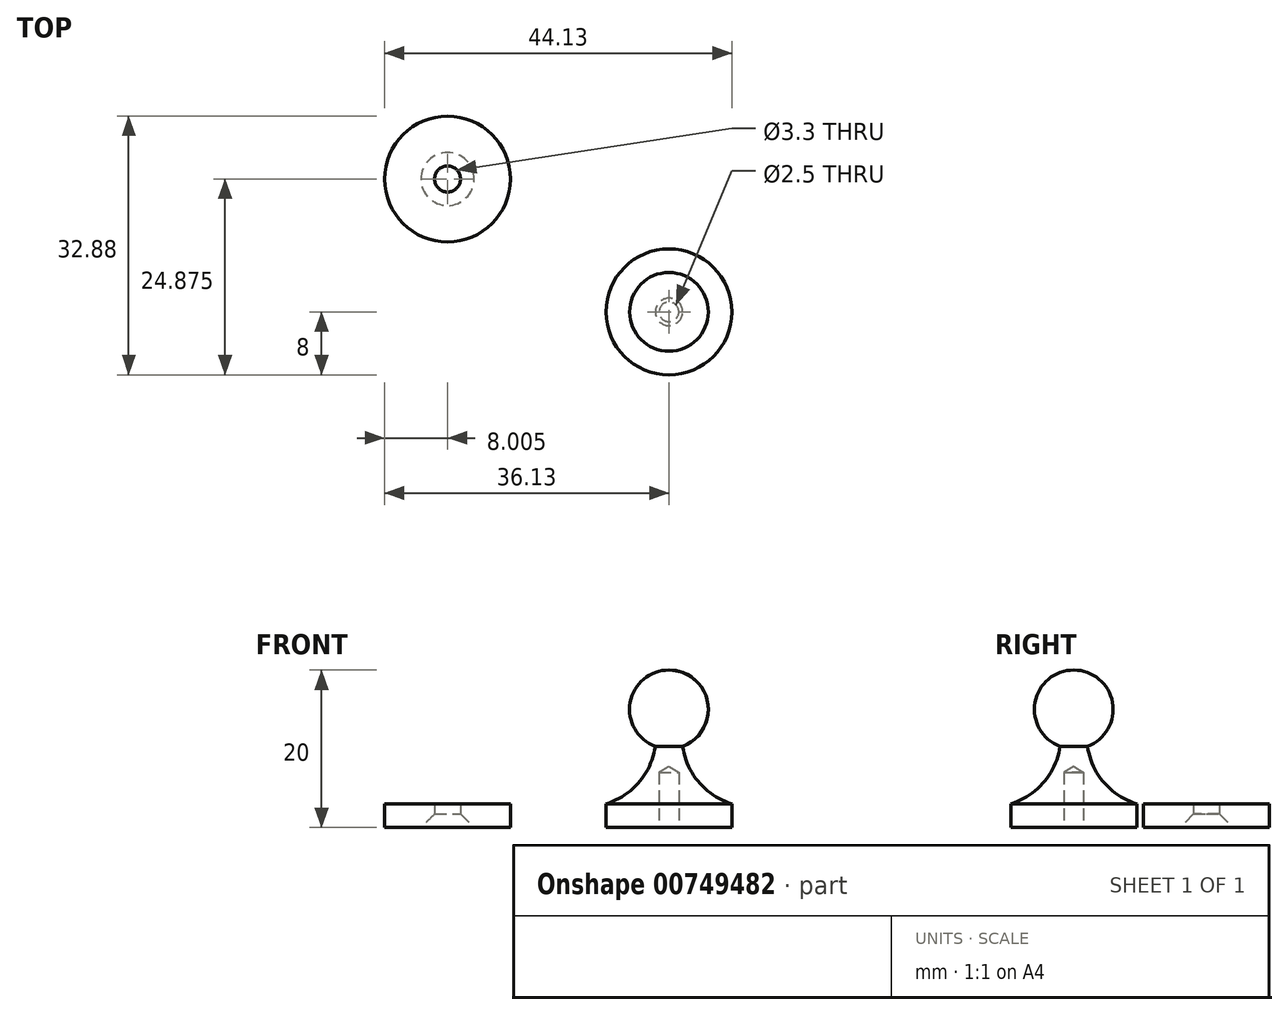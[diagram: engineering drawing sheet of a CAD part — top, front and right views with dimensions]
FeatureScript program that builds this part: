
annotation { "Feature Type Name" : "Feature", "Feature Type Description" : "" }
export const myFeature = defineFeature(function(context is Context, id is Id, definition is map)
    precondition{}
    {
        {
            var Q0;
            Q0=qCreatedBy(makeId("Front.planeOp"),FACE);
            var sketch = newSketch(context, id + "F0", { "sketchPlane" : qUnion([Q0])});
            skLineSegment(sketch, "E0", {"start": v(0, 0) * mm, "end": v(-8, 0) * mm});
            skLineSegment(sketch, "E1", {"start": v(-8, 0) * mm, "end": v(-8, 3) * mm});
            skArc(sketch, "E2", {"start": v(0, 20) * mm, "mid": v(-4.92, 15.88) * mm, "end": v(-1.74, 10.31) * mm});
            skArc(sketch, "E3", {"start": v(-8, 3) * mm, "mid": v(-3.8, 5.75) * mm, "end": v(-1.74, 10.31) * mm});
            skLineSegment(sketch, "E4", {"start": v(0, 20) * mm, "end": v(0, 0) * mm});
            skSolve(sketch);
        }
        {
            var Q0;
            Q0=makeQuery(id+"F0.imprint","IMPRINT",FACE,{"disambiguationData":[TD([[makeQuery(id+"F0.imprint","IMPRINT",EDGE,{"derivedFrom":sQuery(id+"F0.wireOp",EDGE,"E0")}),-1.0]])]});
            var Q1;
            Q1=sQuery(id+"F0.wireOp",EDGE,"E4");
            revolve(context, id + "F1", {"surfaceOperationType" : NewSurfaceOperationType.NEW, "entities" : qUnion([Q0]), "axis" : qUnion([Q1]), "revolveType" : RevolveType.FULL});
        }
        {
            var Q0;
            Q0=makeQuery(id+"F1.opRevolve","SWEPT_FACE",FACE,{"disambiguationData":[OSD([sQuery(id+"F0.wireOp",EDGE,"E0")])]});
            var sketch = newSketch(context, id + "F2", { "sketchPlane" : qUnion([Q0])});
            skPoint(sketch, "E5", {"position": v(0, 0) * mm});
            skSolve(sketch);
        }
        {
            var Q0;
            Q0=sQuery(id+"F2.wireOp",VERTEX,"E5");
            var Q1;
            Q1=makeQuery(id+"F1.opRevolve","SWEPT_BODY",BODY,{"disambiguationData":[OSD([sQuery(id+"F0.wireOp",EDGE,"E0"),sQuery(id+"F0.wireOp",EDGE,"E1"),sQuery(id+"F0.wireOp",EDGE,"E2"),sQuery(id+"F0.wireOp",EDGE,"E3"),sQuery(id+"F0.wireOp",EDGE,"E4")])]});
            hole(context, id + "F3", {"style" : HoleStyle.SIMPLE, "endStyle" : HoleEndStyle.BLIND, "holeDiameter" : 2.5 * mm, "majorDiameter" : 5 * mm, "holeDepth" : 7 * mm, "isTappedThrough" : true, "tappedDepth" : 12 * mm, "tapClearance" : 3, "startFromSketch" : true, "locations" : qUnion([Q0]), "scope" : qUnion([Q1])});
        }
        {
            var Q0;
            Q0=qCreatedBy(makeId("Top.planeOp"),FACE);
            var sketch = newSketch(context, id + "F4", { "sketchPlane" : qUnion([Q0])});
            skCircle(sketch, "E6", {"center": v(-28.13, 16.88) * mm, "radius": 8 * mm});
            skSolve(sketch);
        }
        {
            var Q0;
            Q0=makeQuery(id+"F4.imprint","IMPRINT",FACE,{"disambiguationData":[TD([[makeQuery(id+"F4.imprint","IMPRINT",EDGE,{"derivedFrom":sQuery(id+"F4.wireOp",EDGE,"E6")}),1.0]])]});
            extrude(context, id + "F5", {"entities" : qUnion([Q0]), "depth" : 3 * mm, "offsetDistance" : 25 * mm});
        }
        {
            var Q0;
            Q0=sQuery(id+"F4.wireOp",VERTEX,"E6.center");
            var Q1;
            Q1=makeQuery(id+"F5.opExtrude","SWEPT_BODY",BODY,{"disambiguationData":[OSD([sQuery(id+"F4.wireOp",EDGE,"E6")])]});
            hole(context, id + "F6", {"style" : HoleStyle.C_SINK, "endStyle" : HoleEndStyle.BLIND, "oppositeDirection" : true, "standardTappedOrClearance" : lookupTablePath({ "standard" : "ISO", "fit" : "Normal", "size" : "M3", "type" : "Clearance" }), "standardBlindInLast" : lookupTablePath({ "fit" : "Standard", "standard" : "ISO", "size" : "M3", "type" : "Clearance" }), "holeDiameter" : 3.3 * mm, "cSinkDiameter" : 6.72 * mm, "cSinkAngle" : 90 * degree, "majorDiameter" : 5 * mm, "holeDepth" : 7 * mm, "isTappedThrough" : true, "tappedDepth" : 12 * mm, "tapClearance" : 3, "startFromSketch" : true, "locations" : qUnion([Q0]), "scope" : qUnion([Q1])});
        }
    });
